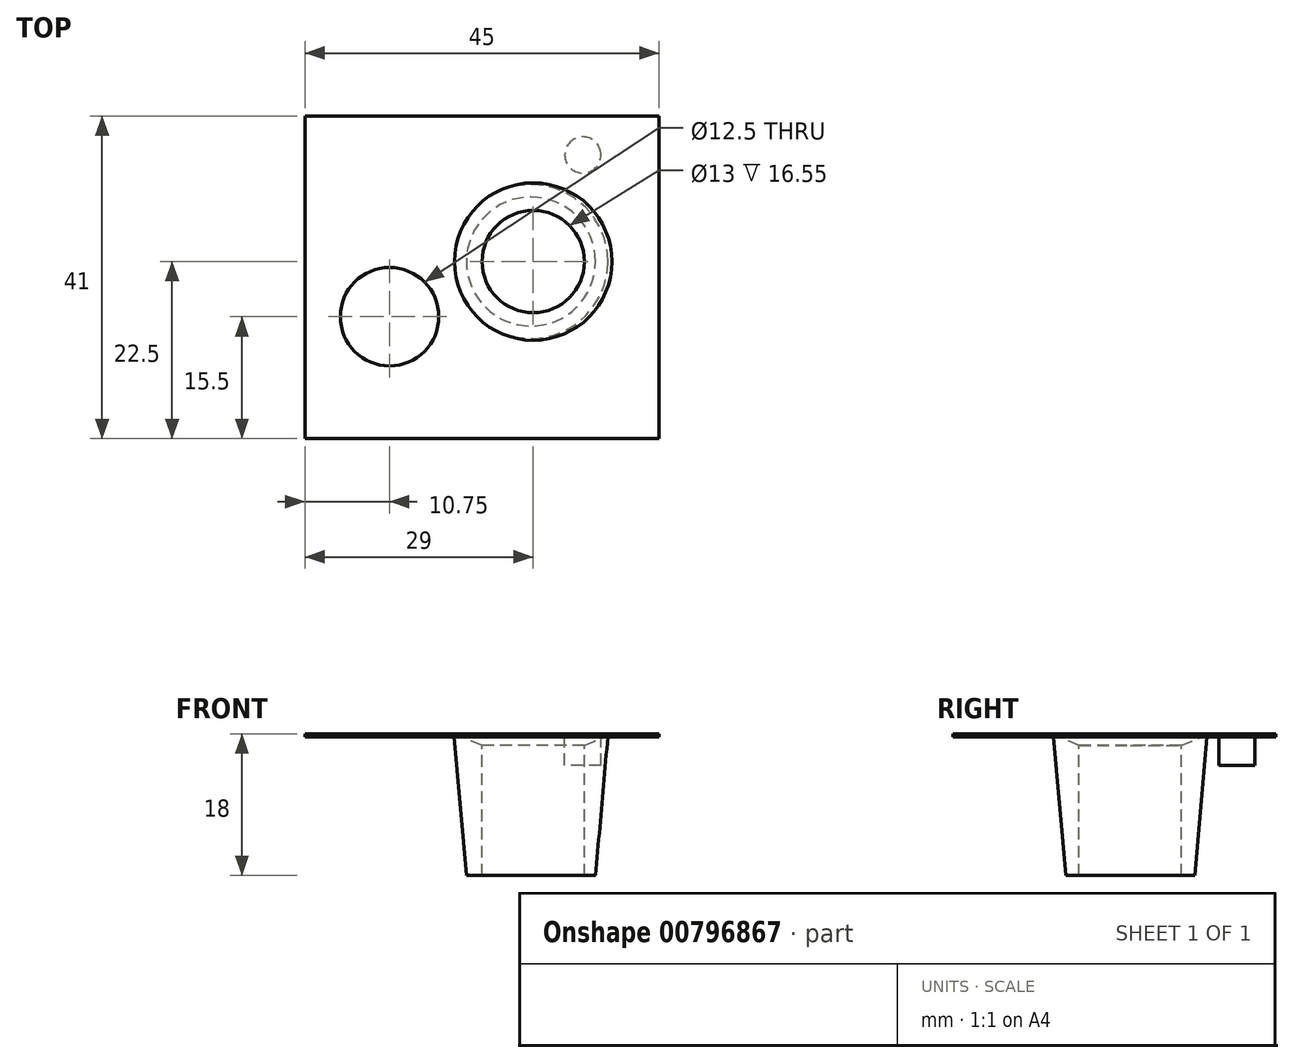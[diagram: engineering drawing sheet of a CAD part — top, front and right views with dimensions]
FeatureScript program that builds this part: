
annotation { "Feature Type Name" : "Feature", "Feature Type Description" : "" }
export const myFeature = defineFeature(function(context is Context, id is Id, definition is map)
    precondition{}
    {
        {
            var Q0;
            Q0=qCreatedBy(makeId("Top.planeOp"),FACE);
            var sketch = newSketch(context, id + "F0", { "sketchPlane" : qUnion([Q0])});
            skLineSegment(sketch, "E0.bottom", {"start": v(22.5, -20.5) * mm, "end": v(-22.5, -20.5) * mm});
            skLineSegment(sketch, "E0.top", {"start": v(22.5, 20.5) * mm, "end": v(-22.5, 20.5) * mm});
            skLineSegment(sketch, "E0.left", {"start": v(22.5, -20.5) * mm, "end": v(22.5, 20.5) * mm});
            skLineSegment(sketch, "E0.right", {"start": v(-22.5, -20.5) * mm, "end": v(-22.5, 20.5) * mm});
            skPoint(sketch, "E0.middle", {"position": v(0, 0) * mm});
            skPoint(sketch, "E1", {"position": v(6.5, 2) * mm});
            skPoint(sketch, "E2", {"position": v(12.65, 15.55) * mm});
            skPoint(sketch, "E3", {"position": v(-11.75, -5) * mm});
            skCircle(sketch, "E4", {"center": v(-11.75, -5) * mm, "radius": 6.25 * mm});
            skSolve(sketch);
        }
        {
            var Q0;
            Q0=makeQuery(id+"F0.imprint","IMPRINT",FACE,{"disambiguationData":[TD([[makeQuery(id+"F0.imprint","IMPRINT",EDGE,{"derivedFrom":sQuery(id+"F0.wireOp",EDGE,"E0.bottom")}),-1.0]])]});
            extrude(context, id + "F1", {"entities" : qUnion([Q0]), "oppositeDirection" : true, "depth" : 0.4 * mm, "offsetDistance" : 25 * mm});
        }
        {
            var Q0;
            Q0=sQuery(id+"F0.wireOp",VERTEX,"E1");
            var Q1;
            Q1=qCreatedBy(makeId("Front.planeOp"),FACE);
            cPlane(context, id + "F2", {"entities" : qUnion([Q0, Q1]), "cplaneType" : CPlaneType.PLANE_POINT, "offset" : 25 * mm, "width" : 150 * mm, "height" : 150 * mm});
        }
        {
            var Q0;
            Q0=qCreatedBy(id+"F2.planeOp",FACE);
            var sketch = newSketch(context, id + "F3", { "sketchPlane" : qUnion([Q0])});
            skLineSegment(sketch, "E5", {"start": v(6.22, 0) * mm, "end": v(6.22, -18) * mm});
            skLineSegment(sketch, "E6", {"start": v(6.22, -18) * mm, "end": v(14.42, -18) * mm});
            skLineSegment(sketch, "E7", {"start": v(6.22, 0) * mm, "end": v(16.02, 0) * mm});
            skLineSegment(sketch, "E8", {"start": v(16.02, 0) * mm, "end": v(14.42, -18) * mm});
            skSolve(sketch);
        }
        {
            var Q0;
            Q0 = qSketchRegion(id + "F3", true);
            var Q1;
            Q1=sQuery(id+"F3.wireOp",EDGE,"E5");
            revolve(context, id + "F4", {"operationType" : NewBodyOperationType.ADD, "surfaceOperationType" : NewSurfaceOperationType.NEW, "entities" : qUnion([Q0]), "axis" : qUnion([Q1]), "revolveType" : RevolveType.FULL});
        }
        {
            var Q0;
            Q0=sQuery(id+"F0.wireOp",VERTEX,"E1");
            var Q1;
            Q1=makeQuery(id+"F1.opExtrude","SWEPT_BODY",BODY,{"disambiguationData":[OSD([sQuery(id+"F0.wireOp",EDGE,"E0.bottom"),sQuery(id+"F0.wireOp",EDGE,"E0.top"),sQuery(id+"F0.wireOp",EDGE,"E0.left"),sQuery(id+"F0.wireOp",EDGE,"E0.right"),sQuery(id+"F0.wireOp",EDGE,"E4")])]});
            hole(context, id + "F5", {"style" : HoleStyle.C_SINK, "endStyle" : HoleEndStyle.THROUGH, "holeDiameter" : 13 * mm, "cSinkDiameter" : 20 * mm, "cSinkAngle" : 135 * degree, "majorDiameter" : 5 * mm, "isTappedThrough" : true, "tappedDepth" : 12 * mm, "tapClearance" : 3, "startFromSketch" : true, "locations" : qUnion([Q0]), "scope" : qUnion([Q1])});
        }
        {
            var Q0;
            Q0=sQuery(id+"F0.wireOp",VERTEX,"E2");
            var Q1;
            Q1=qCreatedBy(makeId("Front.planeOp"),FACE);
            cPlane(context, id + "F6", {"entities" : qUnion([Q0, Q1]), "cplaneType" : CPlaneType.PLANE_POINT, "offset" : 25 * mm, "width" : 150 * mm, "height" : 150 * mm});
        }
        {
            var Q0;
            Q0=qCreatedBy(id+"F6.planeOp",FACE);
            var sketch = newSketch(context, id + "F7", { "sketchPlane" : qUnion([Q0])});
            skLineSegment(sketch, "E9", {"start": v(12.8, 0) * mm, "end": v(12.8, -4) * mm});
            skLineSegment(sketch, "E10", {"start": v(12.8, -4) * mm, "end": v(15.1, -4) * mm});
            skLineSegment(sketch, "E11", {"start": v(15.1, -4) * mm, "end": v(15.1, 0) * mm});
            skLineSegment(sketch, "E12", {"start": v(15.1, 0) * mm, "end": v(12.8, 0) * mm});
            skSolve(sketch);
        }
        {
            var Q0;
            Q0 = qSketchRegion(id + "F7", true);
            var Q1;
            Q1=sQuery(id+"F7.wireOp",EDGE,"E9");
            revolve(context, id + "F8", {"operationType" : NewBodyOperationType.ADD, "surfaceOperationType" : NewSurfaceOperationType.NEW, "entities" : qUnion([Q0]), "axis" : qUnion([Q1]), "revolveType" : RevolveType.FULL});
        }
    });
